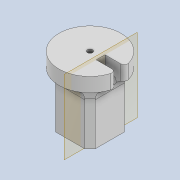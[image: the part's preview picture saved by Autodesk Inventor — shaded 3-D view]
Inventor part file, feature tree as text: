
AUTODESK INVENTOR PART (.ipt)
format: ipt  version: 2020 (Build 240168000, 168)  size: 282,112 bytes
history: native  units: mm
features: extrude x5, sketch x5, fillet x3, chamfer x2, plane x1, projected_geometry x1
ambient origin geometry x8: Origin, YZ Plane, XZ Plane, XY Plane, X Axis, Y Axis, Z Axis, Center Point
bodies: Solid1 (feature_tree)
feature tree (17):
  extrude  "Extrusion1"  Depth=12.5mm
  extrude  "Extrusion2"  Depth=5.0mm
  extrude  "Extrusion3"  Depth=35.0mm
  chamfer  "Chamfer1"  Distance=8.0mm
  fillet  "Fillet1"  Radius=3.0mm
  plane  "Work Plane1"
  extrude  "Extrusion4"  Depth=2.0mm TaperAngle=45.0deg
  extrude  "Extrusion5"  Depth=6.0mm
  chamfer  "Chamfer2"  Distance=4.0mm
  fillet  "Fillet2"  Radius=2.0mm
  fillet  "Fillet3"  Radius=100.0mm
  sketch  "Sketch1"  dims[d0=12.5mm d1=12.5mm]
  sketch  "Sketch2"  dims[d2=5.0mm d3=5.0mm]
  projected_geometry  "Projected Loop1"
  sketch  "Sketch3"  dims[d4=30.0mm d5=0.0mm d6=35.0mm d7=8.0mm d8=0.0mm d9=3.0mm]
  sketch  "Sketch4"  dims[d10=8.0mm d11=0.0mm d12=3.0mm d13=2.0mm d14=45.0deg]
  sketch  "Sketch5"  dims[d15=6.0mm d16=6.0mm d17=4.0mm d18=2.0mm d19=100.0mm d20=0.0mm d21=10.0mm d22=5.0mm d23=100.0mm d24=0.0mm d25=3.0mm d26=2.0mm d27=45.0deg d28=1.0mm d29=2.0mm]
